FCSTD DOCUMENT  (FreeCAD 0.19R24276 (Git))
Label: logo
License: All rights reserved
LicenseURL: http://en.wikipedia.org/wiki/All_rights_reserved
objects: Part::Part2DObjectPython×9
note: 9 computed .brp shape members not serialized (recipe doc carries the construction recipe); baked Part::Feature solids carry a one-line shape summary decoded from their .brp

FEATURE [Part::Part2DObjectPython] Line  # Draft 2D object (typed FeaturePython)
  Area = 0
  ChamferSize = 0
  Closed = false
  End = (-34,40,0)
  FilletRadius = 0
  Length = 14
  MakeFace = false
  Placement = pos=(-20,40,0) rot=(0,0,1;0rad)
  Points = (2) [(0,0,0),(-14,0,0)]
  Start = (-20,40,0)
  Subdivisions = 0
FEATURE [Part::Part2DObjectPython] Arc001  # Draft 2D object (typed FeaturePython)
  Area = 0
  FirstAngle = 90
  LastAngle = 180
  MakeFace = false
  Placement = pos=(-34,33,0) rot=(0,0,1;0rad)
  Radius = 7
FEATURE [Part::Part2DObjectPython] Wire  # Draft 2D object (typed FeaturePython)
  Area = 0
  ChamferSize = 0
  Closed = false
  End = (14,-10,0)
  FilletRadius = 0
  Length = 114
  MakeFace = false
  Placement = pos=(-20,40,0) rot=(0,0,1;0rad)
  Points = (6) [(0,0,0),(0,-22,0),(18,-22,0),(18,-7,0),(34,-7,0),(34,-50,0)]
  Start = (-20,40,0)
  Subdivisions = 0
FEATURE [Part::Part2DObjectPython] Arc  # Draft 2D object (typed FeaturePython)
  Area = 0
  FirstAngle = -90
  LastAngle = 0
  MakeFace = false
  Placement = pos=(2,-35,0) rot=(0,0,1;0rad)
  Radius = 12
FEATURE [Part::Part2DObjectPython] Line002  # Draft 2D object (typed FeaturePython)
  Area = 0
  ChamferSize = 0
  Closed = false
  End = (14,-35,0)
  FilletRadius = 0
  Length = 25
  MakeFace = false
  Placement = pos=(14,-10,0) rot=(0,0,1;0rad)
  Points = (2) [(0,0,0),(-7.10543e-15,-25,0)]
  Start = (14,-10,0)
  Subdivisions = 0
FEATURE [Part::Part2DObjectPython] Line001  # Draft 2D object (typed FeaturePython)
  Area = 0
  ChamferSize = 0
  Closed = false
  End = (-29,-47,0)
  FilletRadius = 0
  Length = 31
  MakeFace = false
  Placement = pos=(2,-47,0) rot=(0,0,1;0rad)
  Points = (2) [(0,0,0),(-31,0,0)]
  Start = (2,-47,0)
  Subdivisions = 0
FEATURE [Part::Part2DObjectPython] Arc002  # Draft 2D object (typed FeaturePython)
  Area = 0
  FirstAngle = 180
  LastAngle = 270
  MakeFace = false
  Placement = pos=(-30,-36,0) rot=(0,0,1;0rad)
  Radius = 11
FEATURE [Part::Part2DObjectPython] Line003  # Draft 2D object (typed FeaturePython)
  Area = 0
  ChamferSize = 0
  Closed = false
  End = (-41,-36,0)
  FilletRadius = 0
  Length = 69
  MakeFace = false
  Placement = pos=(-41,33,0) rot=(0,0,1;0rad)
  Points = (2) [(0,0,0),(0,-69,0)]
  Start = (-41,33,0)
  Subdivisions = 0
FEATURE [Part::Part2DObjectPython] Line004  # Draft 2D object (typed FeaturePython)
  Area = 0
  ChamferSize = 0
  Closed = false
  End = (-29,-47,0)
  FilletRadius = 0
  Length = 1
  MakeFace = false
  Placement = pos=(-30,-47,0) rot=(0,0,1;0rad)
  Points = (2) [(0,0,0),(1,0,0)]
  Start = (-30,-47,0)
  Subdivisions = 0
